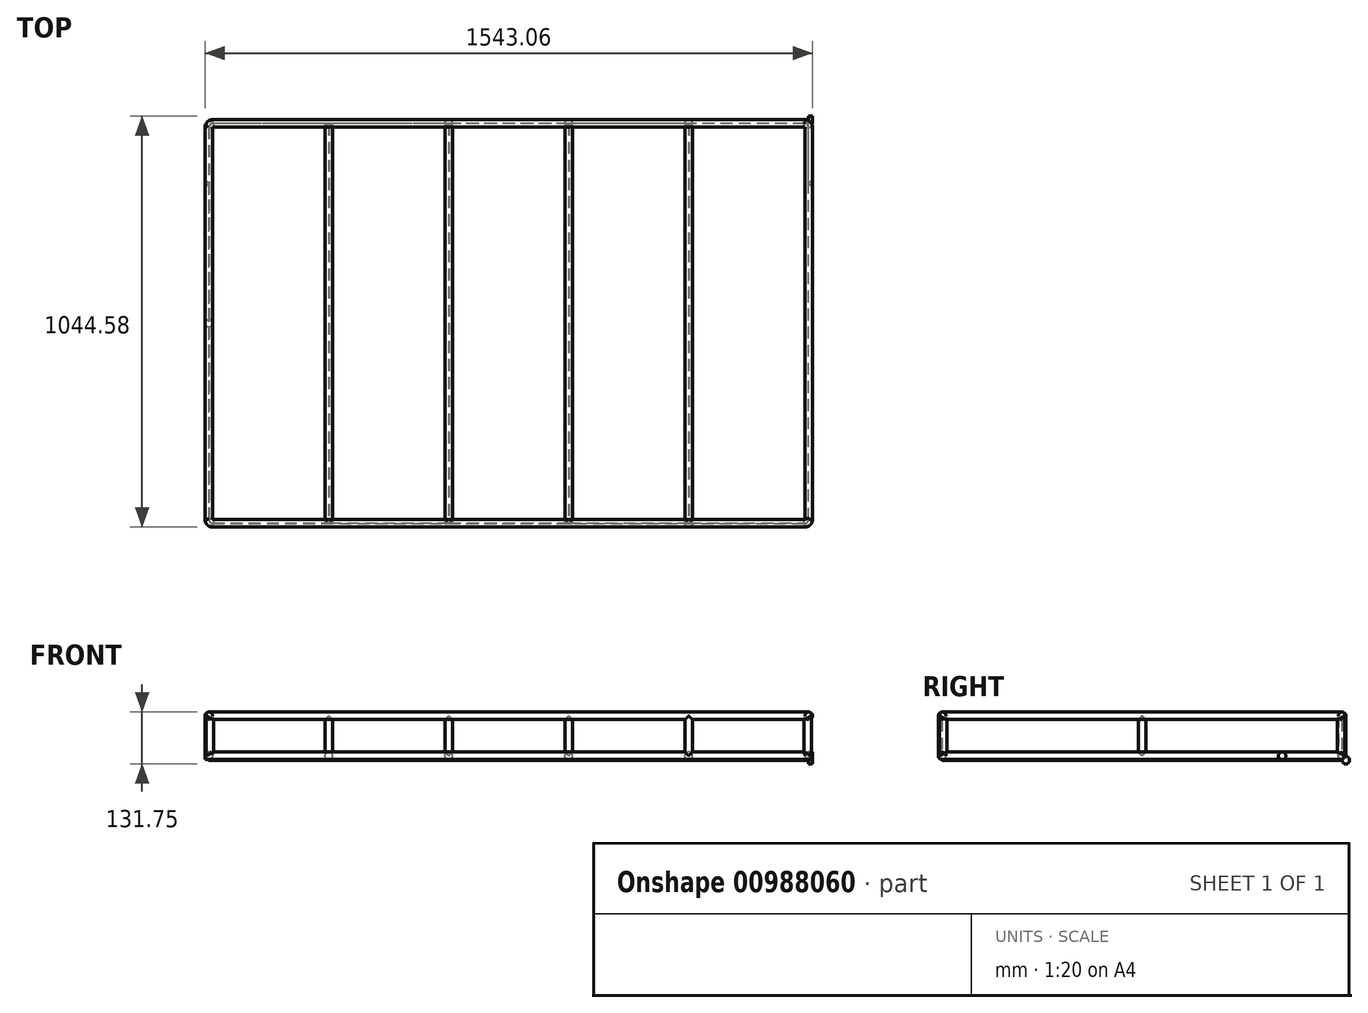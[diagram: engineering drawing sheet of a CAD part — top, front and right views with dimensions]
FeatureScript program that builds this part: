
annotation { "Feature Type Name" : "Feature", "Feature Type Description" : "" }
export const myFeature = defineFeature(function(context is Context, id is Id, definition is map)
    precondition{}
    {
        {
            var Q0;
            Q0=qCreatedBy(makeId("Top.planeOp"),FACE);
            var sketch = newSketch(context, id + "F0", { "sketchPlane" : qUnion([Q0])});
            skLineSegment(sketch, "E0.top", {"start": v(152.4, -1016) * mm, "end": v(1371.6, -1016) * mm});
            skLineSegment(sketch, "E0.left", {"start": v(0, -152.4) * mm, "end": v(0, -863.6) * mm});
            skLineSegment(sketch, "E1", {"start": v(1524, -152.4) * mm, "end": v(1524, -863.6) * mm});
            skLineSegment(sketch, "E2.direction1", {"start": v(0, -330.2) * mm, "end": v(25.4, -330.2) * mm, "construction": true});
            skLineSegment(sketch, "E2.direction2", {"start": v(0, -330.2) * mm, "end": v(0, -668.78) * mm, "construction": true});
            skLineSegment(sketch, "E3.1.0.0", {"start": v(304.8, 0) * mm, "end": v(304.8, -1016) * mm});
            skLineSegment(sketch, "E3.2.0.0", {"start": v(609.6, 0) * mm, "end": v(609.6, -1016) * mm});
            skLineSegment(sketch, "E3.3.0.0", {"start": v(914.4, 0) * mm, "end": v(914.4, -1016) * mm});
            skLineSegment(sketch, "E3.4.0.0", {"start": v(1219.2, 0) * mm, "end": v(1219.2, -1016) * mm});
            skLineSegment(sketch, "E3.direction1", {"start": v(0, -1016) * mm, "end": v(304.8, -1016) * mm, "construction": true});
            skCircle(sketch, "E4", {"center": v(304.8, 0) * mm, "radius": 9.53 * mm});
            skCircle(sketch, "E5", {"center": v(609.6, 0) * mm, "radius": 9.53 * mm});
            skCircle(sketch, "E6", {"center": v(914.4, 0) * mm, "radius": 9.53 * mm});
            skCircle(sketch, "E7", {"center": v(1219.2, 0) * mm, "radius": 9.53 * mm});
            skCircle(sketch, "E8", {"center": v(1524, -508) * mm, "radius": 9.53 * mm});
            skCircle(sketch, "E9", {"center": v(1219.2, -1016) * mm, "radius": 9.52 * mm});
            skCircle(sketch, "E10", {"center": v(914.4, -1016) * mm, "radius": 9.52 * mm});
            skCircle(sketch, "E11", {"center": v(609.6, -1016) * mm, "radius": 9.52 * mm});
            skCircle(sketch, "E12", {"center": v(304.8, -1016) * mm, "radius": 9.53 * mm});
            skCircle(sketch, "E13", {"center": v(0, -508) * mm, "radius": 9.53 * mm});
            skLineSegment(sketch, "E14", {"start": v(0, -1006.48) * mm, "end": v(0, -9.53) * mm});
            skLineSegment(sketch, "E15", {"start": v(9.53, 0) * mm, "end": v(1514.47, 0) * mm});
            skLineSegment(sketch, "E16", {"start": v(1524, -9.53) * mm, "end": v(1524, -1006.48) * mm});
            skLineSegment(sketch, "E17", {"start": v(1514.48, -1016) * mm, "end": v(9.53, -1016) * mm});
            skPoint(sketch, "E18.visualSharp", {"position": v(0, 0) * mm});
            skArc(sketch, "E19.filletArc", {"start": v(9.53, 0) * mm, "mid": v(2.79, -2.79) * mm, "end": v(0, -9.53) * mm});
            skPoint(sketch, "E20.visualSharp", {"position": v(1524, 0) * mm});
            skArc(sketch, "E20.filletArc", {"start": v(1524, -9.52) * mm, "mid": v(1521.21, -2.79) * mm, "end": v(1514.47, 0) * mm});
            skPoint(sketch, "E21.visualSharp", {"position": v(1524, -1016) * mm});
            skArc(sketch, "E21.filletArc", {"start": v(1514.48, -1016) * mm, "mid": v(1521.21, -1013.21) * mm, "end": v(1524, -1006.48) * mm});
            skPoint(sketch, "E22.visualSharp", {"position": v(0, -1016) * mm});
            skArc(sketch, "E22.filletArc", {"start": v(0, -1006.48) * mm, "mid": v(2.79, -1013.21) * mm, "end": v(9.53, -1016) * mm});
            skCircle(sketch, "E23", {"center": v(2.79, -2.79) * mm, "radius": 9.53 * mm});
            skCircle(sketch, "E24", {"center": v(2.79, -1013.21) * mm, "radius": 9.53 * mm});
            skCircle(sketch, "E25", {"center": v(1521.21, -1013.21) * mm, "radius": 9.53 * mm});
            skCircle(sketch, "E26", {"center": v(1521.21, -2.79) * mm, "radius": 9.53 * mm});
            skSolve(sketch);
        }
        {
            var Q0;
            Q0=qCreatedBy(makeId("Front.planeOp"),FACE);
            cPlane(context, id + "F1", {"entities" : qUnion([Q0]), "cplaneType" : CPlaneType.OFFSET, "offset" : 609.6 * mm, "width" : 152.4 * mm, "height" : 152.4 * mm});
        }
        {
            var Q0;
            Q0=qCreatedBy(id+"F1.planeOp",FACE);
            var sketch = newSketch(context, id + "F2", { "sketchPlane" : qUnion([Q0])});
            skCircle(sketch, "E27", {"center": v(0, 0) * mm, "radius": 9.53 * mm});
            skCircle(sketch, "E28.1.0.0", {"center": v(304.8, 0) * mm, "radius": 9.53 * mm});
            skCircle(sketch, "E28.2.0.0", {"center": v(609.6, 0) * mm, "radius": 9.53 * mm});
            skCircle(sketch, "E28.3.0.0", {"center": v(914.4, 0) * mm, "radius": 9.53 * mm});
            skCircle(sketch, "E28.4.0.0", {"center": v(1219.2, 0) * mm, "radius": 9.53 * mm});
            skLineSegment(sketch, "E28.direction1", {"start": v(0, 0) * mm, "end": v(304.8, 0) * mm, "construction": true});
            skSolve(sketch);
        }
        {
            var Q0;
            Q0=makeQuery(id+"F2.imprint","IMPRINT",FACE,{"disambiguationData":[TD([[makeQuery(id+"F2.imprint","IMPRINT",EDGE,{"derivedFrom":sQuery(id+"F2.wireOp",EDGE,"E27")}),1.0]])]});
            var Q1;
            Q1=sQuery(id+"F0.wireOp",EDGE,"E14");
            var Q2;
            Q2=sQuery(id+"F0.wireOp",EDGE,"E19.filletArc");
            var Q3;
            Q3=sQuery(id+"F0.wireOp",EDGE,"E15");
            var Q4;
            Q4=sQuery(id+"F0.wireOp",EDGE,"E20.filletArc");
            var Q5;
            Q5=sQuery(id+"F0.wireOp",EDGE,"E16");
            var Q6;
            Q6=sQuery(id+"F0.wireOp",EDGE,"E21.filletArc");
            var Q7;
            Q7=sQuery(id+"F0.wireOp",EDGE,"E17");
            var Q8;
            Q8=sQuery(id+"F0.wireOp",EDGE,"E22.filletArc");
            sweep(context, id + "F3", {"profiles" : qUnion([Q0]), "path" : qUnion([Q1, Q2, Q3, Q4, Q5, Q6, Q7, Q8])});
        }
        {
            var Q0;
            Q0=makeQuery(id+"F2.imprint","IMPRINT",FACE,{"disambiguationData":[TD([[makeQuery(id+"F2.imprint","IMPRINT",EDGE,{"derivedFrom":sQuery(id+"F2.wireOp",EDGE,"E28.1.0.0")}),1.0]])]});
            var Q1;
            Q1=makeQuery(id+"F2.imprint","IMPRINT",FACE,{"disambiguationData":[TD([[makeQuery(id+"F2.imprint","IMPRINT",EDGE,{"derivedFrom":sQuery(id+"F2.wireOp",EDGE,"E28.2.0.0")}),1.0]])]});
            var Q2;
            Q2=makeQuery(id+"F2.imprint","IMPRINT",FACE,{"disambiguationData":[TD([[makeQuery(id+"F2.imprint","IMPRINT",EDGE,{"derivedFrom":sQuery(id+"F2.wireOp",EDGE,"E28.3.0.0")}),1.0]])]});
            var Q3;
            Q3=makeQuery(id+"F2.imprint","IMPRINT",FACE,{"disambiguationData":[TD([[makeQuery(id+"F2.imprint","IMPRINT",EDGE,{"derivedFrom":sQuery(id+"F2.wireOp",EDGE,"E28.4.0.0")}),1.0]])]});
            var Q4;
            Q4=sQuery(id+"F0.wireOp",EDGE,"E3.1.0.0");
            sweep(context, id + "F4", {"operationType" : NewBodyOperationType.ADD, "profiles" : qUnion([Q0, Q1, Q2, Q3]), "path" : qUnion([Q4])});
        }
        {
            var Q0;
            Q0=qCreatedBy(makeId("Top.planeOp"),FACE);
            cPlane(context, id + "F5", {"entities" : qUnion([Q0]), "cplaneType" : CPlaneType.OFFSET, "offset" : 9.5 * mm, "oppositeDirection" : true, "width" : 152.4 * mm, "height" : 152.4 * mm});
        }
        {
            var Q0;
            Q0=qCreatedBy(makeId("Top.planeOp"),FACE);
            cPlane(context, id + "F6", {"entities" : qUnion([Q0]), "cplaneType" : CPlaneType.OFFSET, "offset" : 101.6 * mm, "width" : 152.4 * mm, "height" : 152.4 * mm});
        }
        {
            var Q0;
            Q0=qCreatedBy(id+"F6.planeOp",FACE);
            var sketch = newSketch(context, id + "F7", { "sketchPlane" : qUnion([Q0])});
            skPoint(sketch, "E29.visualSharp", {"position": v(0, 0) * mm});
            skPoint(sketch, "E30.visualSharp", {"position": v(1524, 0) * mm});
            skPoint(sketch, "E31.visualSharp", {"position": v(1524, -1016) * mm});
            skPoint(sketch, "E32.visualSharp", {"position": v(0, -1016) * mm});
            skLineSegment(sketch, "E33", {"start": v(0, -1006.48) * mm, "end": v(0, -9.53) * mm});
            skLineSegment(sketch, "E34", {"start": v(9.53, 0) * mm, "end": v(1514.48, 0) * mm});
            skLineSegment(sketch, "E35", {"start": v(1524, -9.53) * mm, "end": v(1524, -1006.48) * mm});
            skLineSegment(sketch, "E36", {"start": v(1514.48, -1016) * mm, "end": v(9.53, -1016) * mm});
            skArc(sketch, "E37.filletArc", {"start": v(9.53, 0) * mm, "mid": v(2.79, -2.79) * mm, "end": v(0, -9.53) * mm});
            skArc(sketch, "E38.filletArc", {"start": v(1524, -9.53) * mm, "mid": v(1521.21, -2.79) * mm, "end": v(1514.48, 0) * mm});
            skArc(sketch, "E39.filletArc", {"start": v(1514.48, -1016) * mm, "mid": v(1521.21, -1013.21) * mm, "end": v(1524, -1006.48) * mm});
            skArc(sketch, "E40.filletArc", {"start": v(0, -1006.48) * mm, "mid": v(2.79, -1013.21) * mm, "end": v(9.53, -1016) * mm});
            skSolve(sketch);
        }
        {
            var Q0;
            Q0=qCreatedBy(id+"F1.planeOp",FACE);
            var sketch = newSketch(context, id + "F8", { "sketchPlane" : qUnion([Q0])});
            skLineSegment(sketch, "E41", {"start": v(0, 0) * mm, "end": v(0, 101.6) * mm, "construction": true});
            skCircle(sketch, "E42", {"center": v(0, 101.6) * mm, "radius": 9.53 * mm});
            skSolve(sketch);
        }
        {
            var Q0;
            {var subQ0=sQuery(id+"F0.wireOp",EDGE,"E19.filletArc");Q0=makeQuery(id+"F0.imprint","IMPRINT",FACE,{"disambiguationData":[TD([[makeQuery(id+"F0.imprint","IMPRINT",EDGE,{"derivedFrom":subQ0}),1.0]])]});}
            var Q1;
            {var subQ0=sQuery(id+"F0.wireOp",EDGE,"E19.filletArc");Q1=makeQuery(id+"F0.imprint","IMPRINT",FACE,{"disambiguationData":[TD([[makeQuery(id+"F0.imprint","IMPRINT",EDGE,{"derivedFrom":subQ0}),-1.0]])]});}
            var Q2;
            {var subQ0=sQuery(id+"F0.wireOp",EDGE,"E15");var subQ1=sQuery(id+"F0.wireOp",EDGE,"E3.1.0.0");var subQ2=makeQuery(id+"F0.imprint","INTERSECT",VERTEX,{"derivedFrom":[subQ1,subQ0]});Q2=makeQuery(id+"F0.imprint","IMPRINT",FACE,{"disambiguationData":[TD([[makeQuery(id+"F0.imprint","IMPRINT",EDGE,{"disambiguationData":[TD([[subQ2,-1.0]])],"derivedFrom":subQ1}),1.0]])]});}
            var Q3;
            {var subQ0=sQuery(id+"F0.wireOp",EDGE,"E15");var subQ1=sQuery(id+"F0.wireOp",EDGE,"E3.1.0.0");var subQ2=makeQuery(id+"F0.imprint","INTERSECT",VERTEX,{"derivedFrom":[subQ1,subQ0]});Q3=makeQuery(id+"F0.imprint","IMPRINT",FACE,{"disambiguationData":[TD([[makeQuery(id+"F0.imprint","IMPRINT",EDGE,{"disambiguationData":[TD([[subQ2,-1.0]])],"derivedFrom":subQ1}),-1.0]])]});}
            var Q4;
            {var subQ0=sQuery(id+"F0.wireOp",EDGE,"E15");var subQ1=sQuery(id+"F0.wireOp",EDGE,"E4");var subQ2=makeQuery(id+"F0.imprint","INTERSECT",VERTEX,{"disambiguationData":[OD(0.0)],"derivedFrom":[subQ1,subQ0]});Q4=makeQuery(id+"F0.imprint","IMPRINT",FACE,{"disambiguationData":[TD([[makeQuery(id+"F0.imprint","IMPRINT",EDGE,{"disambiguationData":[TD([[subQ2,1.0]])],"derivedFrom":subQ1}),1.0]])]});}
            var Q5;
            {var subQ0=sQuery(id+"F0.wireOp",EDGE,"E15");var subQ1=sQuery(id+"F0.wireOp",EDGE,"E3.2.0.0");var subQ2=makeQuery(id+"F0.imprint","INTERSECT",VERTEX,{"derivedFrom":[subQ1,subQ0]});Q5=makeQuery(id+"F0.imprint","IMPRINT",FACE,{"disambiguationData":[TD([[makeQuery(id+"F0.imprint","IMPRINT",EDGE,{"disambiguationData":[TD([[subQ2,-1.0]])],"derivedFrom":subQ1}),1.0]])]});}
            var Q6;
            {var subQ0=sQuery(id+"F0.wireOp",EDGE,"E15");var subQ1=sQuery(id+"F0.wireOp",EDGE,"E3.2.0.0");var subQ2=makeQuery(id+"F0.imprint","INTERSECT",VERTEX,{"derivedFrom":[subQ1,subQ0]});Q6=makeQuery(id+"F0.imprint","IMPRINT",FACE,{"disambiguationData":[TD([[makeQuery(id+"F0.imprint","IMPRINT",EDGE,{"disambiguationData":[TD([[subQ2,-1.0]])],"derivedFrom":subQ1}),-1.0]])]});}
            var Q7;
            {var subQ0=sQuery(id+"F0.wireOp",EDGE,"E15");var subQ1=sQuery(id+"F0.wireOp",EDGE,"E5");var subQ2=makeQuery(id+"F0.imprint","INTERSECT",VERTEX,{"disambiguationData":[OD(0.0)],"derivedFrom":[subQ1,subQ0]});Q7=makeQuery(id+"F0.imprint","IMPRINT",FACE,{"disambiguationData":[TD([[makeQuery(id+"F0.imprint","IMPRINT",EDGE,{"disambiguationData":[TD([[subQ2,1.0]])],"derivedFrom":subQ1}),1.0]])]});}
            var Q8;
            {var subQ0=sQuery(id+"F0.wireOp",EDGE,"E15");var subQ1=sQuery(id+"F0.wireOp",EDGE,"E3.3.0.0");var subQ2=makeQuery(id+"F0.imprint","INTERSECT",VERTEX,{"derivedFrom":[subQ1,subQ0]});Q8=makeQuery(id+"F0.imprint","IMPRINT",FACE,{"disambiguationData":[TD([[makeQuery(id+"F0.imprint","IMPRINT",EDGE,{"disambiguationData":[TD([[subQ2,-1.0]])],"derivedFrom":subQ1}),1.0]])]});}
            var Q9;
            {var subQ0=sQuery(id+"F0.wireOp",EDGE,"E15");var subQ1=sQuery(id+"F0.wireOp",EDGE,"E3.3.0.0");var subQ2=makeQuery(id+"F0.imprint","INTERSECT",VERTEX,{"derivedFrom":[subQ1,subQ0]});Q9=makeQuery(id+"F0.imprint","IMPRINT",FACE,{"disambiguationData":[TD([[makeQuery(id+"F0.imprint","IMPRINT",EDGE,{"disambiguationData":[TD([[subQ2,-1.0]])],"derivedFrom":subQ1}),-1.0]])]});}
            var Q10;
            {var subQ0=sQuery(id+"F0.wireOp",EDGE,"E15");var subQ1=sQuery(id+"F0.wireOp",EDGE,"E6");var subQ2=makeQuery(id+"F0.imprint","INTERSECT",VERTEX,{"disambiguationData":[OD(0.0)],"derivedFrom":[subQ1,subQ0]});Q10=makeQuery(id+"F0.imprint","IMPRINT",FACE,{"disambiguationData":[TD([[makeQuery(id+"F0.imprint","IMPRINT",EDGE,{"disambiguationData":[TD([[subQ2,1.0]])],"derivedFrom":subQ1}),1.0]])]});}
            var Q11;
            {var subQ0=sQuery(id+"F0.wireOp",EDGE,"E15");var subQ1=sQuery(id+"F0.wireOp",EDGE,"E3.4.0.0");var subQ2=makeQuery(id+"F0.imprint","INTERSECT",VERTEX,{"derivedFrom":[subQ1,subQ0]});Q11=makeQuery(id+"F0.imprint","IMPRINT",FACE,{"disambiguationData":[TD([[makeQuery(id+"F0.imprint","IMPRINT",EDGE,{"disambiguationData":[TD([[subQ2,-1.0]])],"derivedFrom":subQ1}),1.0]])]});}
            var Q12;
            {var subQ0=sQuery(id+"F0.wireOp",EDGE,"E15");var subQ1=sQuery(id+"F0.wireOp",EDGE,"E3.4.0.0");var subQ2=makeQuery(id+"F0.imprint","INTERSECT",VERTEX,{"derivedFrom":[subQ1,subQ0]});Q12=makeQuery(id+"F0.imprint","IMPRINT",FACE,{"disambiguationData":[TD([[makeQuery(id+"F0.imprint","IMPRINT",EDGE,{"disambiguationData":[TD([[subQ2,-1.0]])],"derivedFrom":subQ1}),-1.0]])]});}
            var Q13;
            {var subQ0=sQuery(id+"F0.wireOp",EDGE,"E15");var subQ1=sQuery(id+"F0.wireOp",EDGE,"E7");var subQ2=makeQuery(id+"F0.imprint","INTERSECT",VERTEX,{"disambiguationData":[OD(0.0)],"derivedFrom":[subQ1,subQ0]});Q13=makeQuery(id+"F0.imprint","IMPRINT",FACE,{"disambiguationData":[TD([[makeQuery(id+"F0.imprint","IMPRINT",EDGE,{"disambiguationData":[TD([[subQ2,1.0]])],"derivedFrom":subQ1}),1.0]])]});}
            var Q14;
            {var subQ0=sQuery(id+"F0.wireOp",EDGE,"E20.filletArc");Q14=makeQuery(id+"F0.imprint","IMPRINT",FACE,{"disambiguationData":[TD([[makeQuery(id+"F0.imprint","IMPRINT",EDGE,{"derivedFrom":subQ0}),1.0]])]});}
            var Q15;
            {var subQ0=sQuery(id+"F0.wireOp",EDGE,"E20.filletArc");Q15=makeQuery(id+"F0.imprint","IMPRINT",FACE,{"disambiguationData":[TD([[makeQuery(id+"F0.imprint","IMPRINT",EDGE,{"derivedFrom":subQ0}),-1.0]])]});}
            var Q16;
            {var subQ0=sQuery(id+"F0.wireOp",EDGE,"E16");var subQ1=sQuery(id+"F0.wireOp",EDGE,"E8");var subQ2=makeQuery(id+"F0.imprint","INTERSECT",VERTEX,{"disambiguationData":[OD(0.0)],"derivedFrom":[subQ1,subQ0]});Q16=makeQuery(id+"F0.imprint","IMPRINT",FACE,{"disambiguationData":[TD([[makeQuery(id+"F0.imprint","IMPRINT",EDGE,{"disambiguationData":[TD([[subQ2,1.0]])],"derivedFrom":subQ1}),1.0]])]});}
            var Q17;
            {var subQ0=sQuery(id+"F0.wireOp",EDGE,"E16");var subQ1=sQuery(id+"F0.wireOp",EDGE,"E8");var subQ2=makeQuery(id+"F0.imprint","INTERSECT",VERTEX,{"disambiguationData":[OD(0.0)],"derivedFrom":[subQ1,subQ0]});Q17=makeQuery(id+"F0.imprint","IMPRINT",FACE,{"disambiguationData":[TD([[makeQuery(id+"F0.imprint","IMPRINT",EDGE,{"disambiguationData":[TD([[subQ2,-1.0]])],"derivedFrom":subQ1}),1.0]])]});}
            var Q18;
            {var subQ0=sQuery(id+"F0.wireOp",EDGE,"E21.filletArc");Q18=makeQuery(id+"F0.imprint","IMPRINT",FACE,{"disambiguationData":[TD([[makeQuery(id+"F0.imprint","IMPRINT",EDGE,{"derivedFrom":subQ0}),-1.0]])]});}
            var Q19;
            {var subQ0=sQuery(id+"F0.wireOp",EDGE,"E21.filletArc");Q19=makeQuery(id+"F0.imprint","IMPRINT",FACE,{"disambiguationData":[TD([[makeQuery(id+"F0.imprint","IMPRINT",EDGE,{"derivedFrom":subQ0}),1.0]])]});}
            var Q20;
            {var subQ0=sQuery(id+"F0.wireOp",EDGE,"E17");var subQ1=sQuery(id+"F0.wireOp",EDGE,"E9");var subQ2=makeQuery(id+"F0.imprint","INTERSECT",VERTEX,{"disambiguationData":[OD(0.0)],"derivedFrom":[subQ1,subQ0]});Q20=makeQuery(id+"F0.imprint","IMPRINT",FACE,{"disambiguationData":[TD([[makeQuery(id+"F0.imprint","IMPRINT",EDGE,{"disambiguationData":[TD([[subQ2,1.0]])],"derivedFrom":subQ1}),1.0]])]});}
            var Q21;
            {var subQ0=sQuery(id+"F0.wireOp",EDGE,"E17");var subQ1=sQuery(id+"F0.wireOp",EDGE,"E3.4.0.0");var subQ2=makeQuery(id+"F0.imprint","INTERSECT",VERTEX,{"derivedFrom":[subQ1,subQ0]});Q21=makeQuery(id+"F0.imprint","IMPRINT",FACE,{"disambiguationData":[TD([[makeQuery(id+"F0.imprint","IMPRINT",EDGE,{"disambiguationData":[TD([[subQ2,1.0]])],"derivedFrom":subQ1}),1.0]])]});}
            var Q22;
            {var subQ0=sQuery(id+"F0.wireOp",EDGE,"E17");var subQ1=sQuery(id+"F0.wireOp",EDGE,"E3.4.0.0");var subQ2=makeQuery(id+"F0.imprint","INTERSECT",VERTEX,{"derivedFrom":[subQ1,subQ0]});Q22=makeQuery(id+"F0.imprint","IMPRINT",FACE,{"disambiguationData":[TD([[makeQuery(id+"F0.imprint","IMPRINT",EDGE,{"disambiguationData":[TD([[subQ2,1.0]])],"derivedFrom":subQ1}),-1.0]])]});}
            var Q23;
            {var subQ0=sQuery(id+"F0.wireOp",EDGE,"E17");var subQ1=sQuery(id+"F0.wireOp",EDGE,"E10");var subQ2=makeQuery(id+"F0.imprint","INTERSECT",VERTEX,{"disambiguationData":[OD(0.0)],"derivedFrom":[subQ1,subQ0]});Q23=makeQuery(id+"F0.imprint","IMPRINT",FACE,{"disambiguationData":[TD([[makeQuery(id+"F0.imprint","IMPRINT",EDGE,{"disambiguationData":[TD([[subQ2,1.0]])],"derivedFrom":subQ1}),1.0]])]});}
            var Q24;
            {var subQ0=sQuery(id+"F0.wireOp",EDGE,"E17");var subQ1=sQuery(id+"F0.wireOp",EDGE,"E3.3.0.0");var subQ2=makeQuery(id+"F0.imprint","INTERSECT",VERTEX,{"derivedFrom":[subQ1,subQ0]});Q24=makeQuery(id+"F0.imprint","IMPRINT",FACE,{"disambiguationData":[TD([[makeQuery(id+"F0.imprint","IMPRINT",EDGE,{"disambiguationData":[TD([[subQ2,1.0]])],"derivedFrom":subQ1}),1.0]])]});}
            var Q25;
            {var subQ0=sQuery(id+"F0.wireOp",EDGE,"E17");var subQ1=sQuery(id+"F0.wireOp",EDGE,"E3.3.0.0");var subQ2=makeQuery(id+"F0.imprint","INTERSECT",VERTEX,{"derivedFrom":[subQ1,subQ0]});Q25=makeQuery(id+"F0.imprint","IMPRINT",FACE,{"disambiguationData":[TD([[makeQuery(id+"F0.imprint","IMPRINT",EDGE,{"disambiguationData":[TD([[subQ2,1.0]])],"derivedFrom":subQ1}),-1.0]])]});}
            var Q26;
            {var subQ0=sQuery(id+"F0.wireOp",EDGE,"E17");var subQ1=sQuery(id+"F0.wireOp",EDGE,"E11");var subQ2=makeQuery(id+"F0.imprint","INTERSECT",VERTEX,{"disambiguationData":[OD(0.0)],"derivedFrom":[subQ1,subQ0]});Q26=makeQuery(id+"F0.imprint","IMPRINT",FACE,{"disambiguationData":[TD([[makeQuery(id+"F0.imprint","IMPRINT",EDGE,{"disambiguationData":[TD([[subQ2,1.0]])],"derivedFrom":subQ1}),1.0]])]});}
            var Q27;
            {var subQ0=sQuery(id+"F0.wireOp",EDGE,"E17");var subQ1=sQuery(id+"F0.wireOp",EDGE,"E3.2.0.0");var subQ2=makeQuery(id+"F0.imprint","INTERSECT",VERTEX,{"derivedFrom":[subQ1,subQ0]});Q27=makeQuery(id+"F0.imprint","IMPRINT",FACE,{"disambiguationData":[TD([[makeQuery(id+"F0.imprint","IMPRINT",EDGE,{"disambiguationData":[TD([[subQ2,1.0]])],"derivedFrom":subQ1}),1.0]])]});}
            var Q28;
            {var subQ0=sQuery(id+"F0.wireOp",EDGE,"E17");var subQ1=sQuery(id+"F0.wireOp",EDGE,"E3.2.0.0");var subQ2=makeQuery(id+"F0.imprint","INTERSECT",VERTEX,{"derivedFrom":[subQ1,subQ0]});Q28=makeQuery(id+"F0.imprint","IMPRINT",FACE,{"disambiguationData":[TD([[makeQuery(id+"F0.imprint","IMPRINT",EDGE,{"disambiguationData":[TD([[subQ2,1.0]])],"derivedFrom":subQ1}),-1.0]])]});}
            var Q29;
            {var subQ0=sQuery(id+"F0.wireOp",EDGE,"E17");var subQ1=sQuery(id+"F0.wireOp",EDGE,"E12");var subQ2=makeQuery(id+"F0.imprint","INTERSECT",VERTEX,{"disambiguationData":[OD(0.0)],"derivedFrom":[subQ1,subQ0]});Q29=makeQuery(id+"F0.imprint","IMPRINT",FACE,{"disambiguationData":[TD([[makeQuery(id+"F0.imprint","IMPRINT",EDGE,{"disambiguationData":[TD([[subQ2,1.0]])],"derivedFrom":subQ1}),1.0]])]});}
            var Q30;
            {var subQ0=sQuery(id+"F0.wireOp",EDGE,"E17");var subQ1=sQuery(id+"F0.wireOp",EDGE,"E3.1.0.0");var subQ2=makeQuery(id+"F0.imprint","INTERSECT",VERTEX,{"derivedFrom":[subQ1,subQ0]});Q30=makeQuery(id+"F0.imprint","IMPRINT",FACE,{"disambiguationData":[TD([[makeQuery(id+"F0.imprint","IMPRINT",EDGE,{"disambiguationData":[TD([[subQ2,1.0]])],"derivedFrom":subQ1}),1.0]])]});}
            var Q31;
            {var subQ0=sQuery(id+"F0.wireOp",EDGE,"E17");var subQ1=sQuery(id+"F0.wireOp",EDGE,"E3.1.0.0");var subQ2=makeQuery(id+"F0.imprint","INTERSECT",VERTEX,{"derivedFrom":[subQ1,subQ0]});Q31=makeQuery(id+"F0.imprint","IMPRINT",FACE,{"disambiguationData":[TD([[makeQuery(id+"F0.imprint","IMPRINT",EDGE,{"disambiguationData":[TD([[subQ2,1.0]])],"derivedFrom":subQ1}),-1.0]])]});}
            var Q32;
            {var subQ0=sQuery(id+"F0.wireOp",EDGE,"E22.filletArc");Q32=makeQuery(id+"F0.imprint","IMPRINT",FACE,{"disambiguationData":[TD([[makeQuery(id+"F0.imprint","IMPRINT",EDGE,{"derivedFrom":subQ0}),-1.0]])]});}
            var Q33;
            {var subQ0=sQuery(id+"F0.wireOp",EDGE,"E22.filletArc");Q33=makeQuery(id+"F0.imprint","IMPRINT",FACE,{"disambiguationData":[TD([[makeQuery(id+"F0.imprint","IMPRINT",EDGE,{"derivedFrom":subQ0}),1.0]])]});}
            var Q34;
            {var subQ0=sQuery(id+"F0.wireOp",EDGE,"E14");var subQ1=sQuery(id+"F0.wireOp",EDGE,"E13");var subQ2=makeQuery(id+"F0.imprint","INTERSECT",VERTEX,{"disambiguationData":[OD(0.0)],"derivedFrom":[subQ1,subQ0]});Q34=makeQuery(id+"F0.imprint","IMPRINT",FACE,{"disambiguationData":[TD([[makeQuery(id+"F0.imprint","IMPRINT",EDGE,{"disambiguationData":[TD([[subQ2,-1.0]])],"derivedFrom":subQ1}),1.0]])]});}
            var Q35;
            {var subQ0=sQuery(id+"F0.wireOp",EDGE,"E14");var subQ1=sQuery(id+"F0.wireOp",EDGE,"E13");var subQ2=makeQuery(id+"F0.imprint","INTERSECT",VERTEX,{"disambiguationData":[OD(0.0)],"derivedFrom":[subQ1,subQ0]});Q35=makeQuery(id+"F0.imprint","IMPRINT",FACE,{"disambiguationData":[TD([[makeQuery(id+"F0.imprint","IMPRINT",EDGE,{"disambiguationData":[TD([[subQ2,1.0]])],"derivedFrom":subQ1}),1.0]])]});}
            extrude(context, id + "F9", {"entities" : qUnion([Q0, Q1, Q2, Q3, Q4, Q5, Q6, Q7, Q8, Q9, Q10, Q11, Q12, Q13, Q14, Q15, Q16, Q17, Q18, Q19, Q20, Q21, Q22, Q23, Q24, Q25, Q26, Q27, Q28, Q29, Q30, Q31, Q32, Q33, Q34, Q35]), "operationType" : NewBodyOperationType.ADD, "depth" : 101.6 * mm, "offsetDistance" : 25.4 * mm});
        }
        {
            var Q0;
            Q0=qCreatedBy(makeId("Right.planeOp"),FACE);
            var sketch = newSketch(context, id + "F10", { "sketchPlane" : qUnion([Q0])});
            skLineSegment(sketch, "E43", {"start": v(0, 0) * mm, "end": v(-152.4, 0) * mm, "construction": true});
            skCircle(sketch, "E44", {"center": v(-152.4, 0) * mm, "radius": 9.53 * mm});
            skSolve(sketch);
        }
        {
            var Q0;
            Q0=makeQuery(id+"F8.imprint","IMPRINT",FACE,{"disambiguationData":[TD([[makeQuery(id+"F8.imprint","IMPRINT",EDGE,{"derivedFrom":sQuery(id+"F8.wireOp",EDGE,"E42")}),1.0]])]});
            var Q1;
            Q1 = qConstructionFilter(qBodyType(qCreatedBy(id + "F7" ,EDGE), BodyType.WIRE), ConstructionObject.NO);
            sweep(context, id + "F11", {"operationType" : NewBodyOperationType.ADD, "profiles" : qUnion([Q0]), "path" : qUnion([Q1])});
        }
        {
            var Q0;
            Q0=qCreatedBy(makeId("Right.planeOp"),FACE);
            cPlane(context, id + "F12", {"entities" : qUnion([Q0]), "cplaneType" : CPlaneType.OFFSET, "offset" : 1524 * mm, "width" : 152.4 * mm, "height" : 152.4 * mm});
        }
        {
            var Q0;
            Q0=qCreatedBy(id+"F12.planeOp",FACE);
            var sketch = newSketch(context, id + "F13", { "sketchPlane" : qUnion([Q0])});
            skLineSegment(sketch, "E45", {"start": v(0, 0) * mm, "end": v(-152.4, 0) * mm, "construction": true});
            skCircle(sketch, "E46", {"center": v(-152.4, 0) * mm, "radius": 9.52 * mm});
            skLineSegment(sketch, "E47", {"start": v(0, 0) * mm, "end": v(9.53, 0) * mm, "construction": true});
            skLineSegment(sketch, "E48", {"start": v(9.53, 0) * mm, "end": v(9.53, -9.52) * mm, "construction": true});
            skLineSegment(sketch, "E49", {"start": v(9.53, -9.52) * mm, "end": v(9.53, -11.1) * mm, "construction": true});
            skCircle(sketch, "E50", {"center": v(9.53, -11.1) * mm, "radius": 9.53 * mm});
            skSolve(sketch);
        }
        {
            var Q0;
            Q0 = qSketchRegion(id + "F13", true);
            extrude(context, id + "F14", {"entities" : qUnion([Q0]), "operationType" : NewBodyOperationType.ADD, "depth" : 9.52 * mm, "offsetDistance" : 25.4 * mm});
        }
        {
            var Q0;
            Q0 = qSketchRegion(id + "F10", true);
            extrude(context, id + "F15", {"entities" : qUnion([Q0]), "operationType" : NewBodyOperationType.ADD, "oppositeDirection" : true, "depth" : 9.52 * mm, "offsetDistance" : 25.4 * mm});
        }
        {
            var Q0;
            Q0=qCreatedBy(makeId("Top.planeOp"),FACE);
            cPlane(context, id + "F16", {"entities" : qUnion([Q0]), "cplaneType" : CPlaneType.OFFSET, "offset" : 9.5 * mm, "oppositeDirection" : true, "width" : 152.4 * mm, "height" : 152.4 * mm});
        }
        {
            var Q0;
            Q0=qCreatedBy(id+"F16.planeOp",FACE);
            var sketch = newSketch(context, id + "F17", { "sketchPlane" : qUnion([Q0])});
            skLineSegment(sketch, "E51", {"start": v(0, -9.53) * mm, "end": v(0, -1006.48) * mm});
            skLineSegment(sketch, "E52", {"start": v(9.53, -1016) * mm, "end": v(1514.48, -1016) * mm});
            skLineSegment(sketch, "E53", {"start": v(1524, -1006.48) * mm, "end": v(1524, -9.53) * mm});
            skLineSegment(sketch, "E54", {"start": v(1514.48, 0) * mm, "end": v(9.53, 0) * mm});
            skPoint(sketch, "E55.visualSharp", {"position": v(0, -1016) * mm});
            skArc(sketch, "E55.filletArc", {"start": v(0, -1006.48) * mm, "mid": v(2.79, -1013.21) * mm, "end": v(9.53, -1016) * mm});
            skPoint(sketch, "E56.visualSharp", {"position": v(1524, -1016) * mm});
            skArc(sketch, "E56.filletArc", {"start": v(1514.48, -1016) * mm, "mid": v(1521.21, -1013.21) * mm, "end": v(1524, -1006.48) * mm});
            skPoint(sketch, "E57.visualSharp", {"position": v(1524, 0) * mm});
            skArc(sketch, "E57.filletArc", {"start": v(1524, -9.53) * mm, "mid": v(1521.21, -2.79) * mm, "end": v(1514.48, 0) * mm});
            skPoint(sketch, "E58.visualSharp", {"position": v(0, 0) * mm});
            skArc(sketch, "E58.filletArc", {"start": v(9.53, 0) * mm, "mid": v(2.79, -2.79) * mm, "end": v(0, -9.53) * mm});
            skSolve(sketch);
        }
        {
            var Q0;
            Q0 = qSketchRegion(id + "F17", true);
            extrude(context, id + "F18", {"entities" : qUnion([Q0]), "operationType" : NewBodyOperationType.ADD, "oppositeDirection" : true, "depth" : 1.59 * mm, "offsetDistance" : 25.4 * mm});
        }
    });
